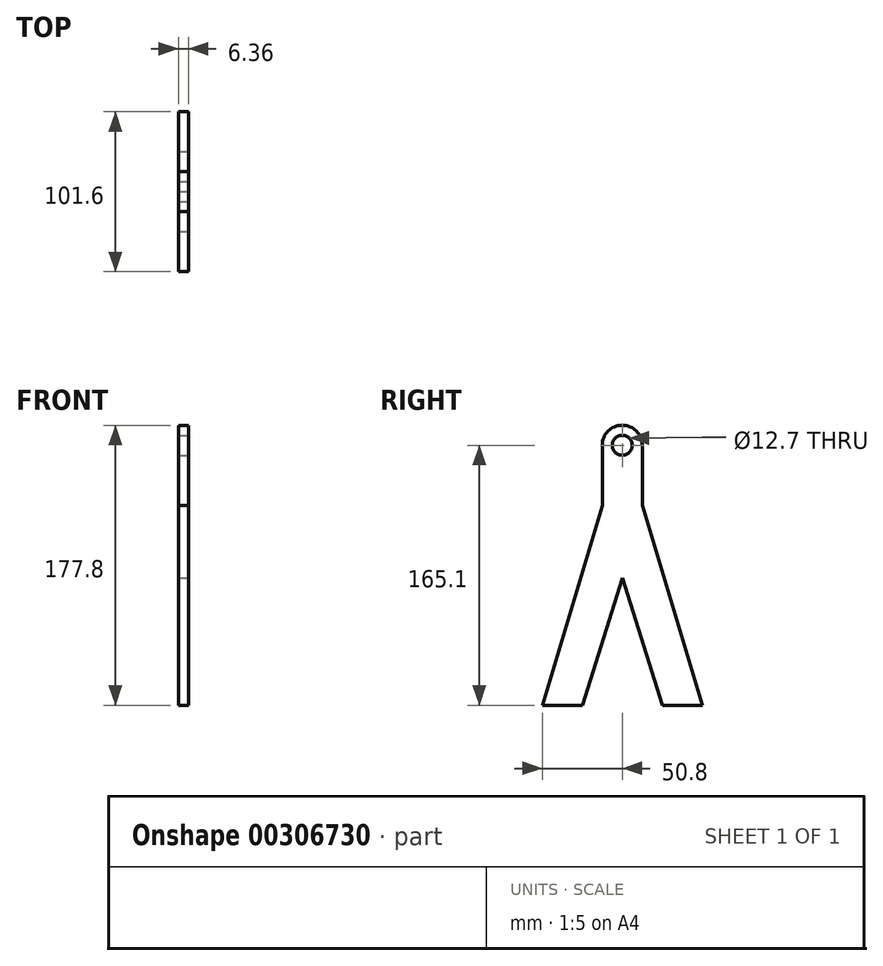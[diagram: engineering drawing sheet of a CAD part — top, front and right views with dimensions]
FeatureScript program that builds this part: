
annotation { "Feature Type Name" : "Feature", "Feature Type Description" : "" }
export const myFeature = defineFeature(function(context is Context, id is Id, definition is map)
    precondition{}
    {
        {
            var Q0;
            Q0=qCreatedBy(makeId("Top.planeOp"),FACE);
            var sketch = newSketch(context, id + "F0", { "sketchPlane" : qUnion([Q0])});
            skLineSegment(sketch, "E0.bottom", {"start": v(3.18, 50.8) * mm, "end": v(-3.17, 50.8) * mm});
            skLineSegment(sketch, "E0.top", {"start": v(3.18, -50.8) * mm, "end": v(-3.17, -50.8) * mm});
            skLineSegment(sketch, "E0.left", {"start": v(3.18, 50.8) * mm, "end": v(3.18, -50.8) * mm});
            skLineSegment(sketch, "E0.right", {"start": v(-3.17, 50.8) * mm, "end": v(-3.17, -50.8) * mm});
            skPoint(sketch, "E0.middle", {"position": v(0, 0) * mm});
            skLineSegment(sketch, "E1.bottom", {"start": v(-3.17, 12.7) * mm, "end": v(3.18, 12.7) * mm});
            skLineSegment(sketch, "E1.top", {"start": v(-3.18, -12.7) * mm, "end": v(3.17, -12.7) * mm});
            skLineSegment(sketch, "E1.left", {"start": v(-3.17, 12.7) * mm, "end": v(-3.18, -12.7) * mm});
            skLineSegment(sketch, "E1.right", {"start": v(3.18, 12.7) * mm, "end": v(3.17, -12.7) * mm});
            skSolve(sketch);
        }
        {
            var Q0;
            Q0=makeQuery(id+"F0.imprint","IMPRINT",FACE,{"disambiguationData":[TD([[makeQuery(id+"F0.imprint","IMPRINT",EDGE,{"derivedFrom":sQuery(id+"F0.wireOp",EDGE,"E1.bottom")}),-1.0]])]});
            extrude(context, id + "F1", {"entities" : qUnion([Q0]), "depth" : 177.8 * mm});
        }
        {
            var Q0;
            Q0=makeQuery(id+"F0.imprint","IMPRINT",FACE,{"disambiguationData":[TD([[makeQuery(id+"F0.imprint","IMPRINT",EDGE,{"derivedFrom":sQuery(id+"F0.wireOp",EDGE,"E0.bottom")}),1.0]])]});
            var Q1;
            {var subQ0=sQuery(id+"F0.wireOp",EDGE,"E0.top");Q1=makeQuery(id+"F0.imprint","IMPRINT",FACE,{"disambiguationData":[TD([[makeQuery(id+"F0.imprint","IMPRINT",EDGE,{"derivedFrom":subQ0}),-1.0]])]});}
            extrude(context, id + "F2", {"entities" : qUnion([Q0, Q1]), "operationType" : NewBodyOperationType.ADD, "depth" : 50.8 * mm});
        }
        {
            var Q0;
            Q0=qCreatedBy(makeId("Right.planeOp"),FACE);
            var sketch = newSketch(context, id + "F3", { "sketchPlane" : qUnion([Q0])});
            skCircle(sketch, "E2", {"center": v(0, 165.1) * mm, "radius": 6.35 * mm});
            skSolve(sketch);
        }
        {
            var Q0;
            Q0=sQuery(id+"F3.wireOp",VERTEX,"E2.center");
            var Q1;
            Q1=makeQuery(id+"F1.opExtrude","SWEPT_BODY",BODY,{"disambiguationData":[OSD([sQuery(id+"F0.wireOp",EDGE,"E1.bottom"),sQuery(id+"F0.wireOp",EDGE,"E1.top"),sQuery(id+"F0.wireOp",EDGE,"E1.left"),sQuery(id+"F0.wireOp",EDGE,"E1.right")])]});
            hole(context, id + "F4", {"style" : HoleStyle.SIMPLE, "endStyle" : HoleEndStyle.THROUGH, "holeDiameter" : 12.7 * mm, "tappedDepth" : 12.7 * mm, "tapClearance" : 3, "locations" : qUnion([Q0]), "scope" : qUnion([Q1])});
        }
        {
            var Q0;
            Q0=sQuery(id+"F3.wireOp",VERTEX,"E2.center");
            var Q1;
            Q1=makeQuery(id+"F1.opExtrude","SWEPT_BODY",BODY,{"disambiguationData":[OSD([sQuery(id+"F0.wireOp",EDGE,"E1.bottom"),sQuery(id+"F0.wireOp",EDGE,"E1.top"),sQuery(id+"F0.wireOp",EDGE,"E1.left"),sQuery(id+"F0.wireOp",EDGE,"E1.right")])]});
            hole(context, id + "F5", {"style" : HoleStyle.SIMPLE, "endStyle" : HoleEndStyle.THROUGH, "oppositeDirection" : true, "holeDiameter" : 12.7 * mm, "tappedDepth" : 12.7 * mm, "tapClearance" : 3, "locations" : qUnion([Q0]), "scope" : qUnion([Q1])});
        }
        {
            var Q0;
            Q0=makeQuery(id+"F1.opExtrude","CAP_EDGE",EDGE,{"disambiguationData":[OSD([sQuery(id+"F0.wireOp",EDGE,"E1.top")])],"isStart":false});
            var Q1;
            Q1=makeQuery(id+"F1.opExtrude","CAP_EDGE",EDGE,{"disambiguationData":[OSD([sQuery(id+"F0.wireOp",EDGE,"E1.bottom")])],"isStart":false});
            fillet(context, id + "F6", {"entities" : qUnion([Q0, Q1]), "radius" : 12.7 * mm, "tangentPropagation" : true, "allowEdgeOverflow" : false});
        }
        {
            var Q0;
            {var subQ0=sQuery(id+"F0.wireOp",EDGE,"E0.top");Q0=makeQuery(id+"F0.imprint","IMPRINT",FACE,{"disambiguationData":[TD([[makeQuery(id+"F0.imprint","IMPRINT",EDGE,{"derivedFrom":subQ0}),-1.0]])]});}
            var Q1;
            {var subQ0=sQuery(id+"F0.wireOp",EDGE,"E0.bottom");Q1=makeQuery(id+"F0.imprint","IMPRINT",FACE,{"disambiguationData":[TD([[makeQuery(id+"F0.imprint","IMPRINT",EDGE,{"derivedFrom":subQ0}),1.0]])]});}
            extrude(context, id + "F7", {"entities" : qUnion([Q0, Q1]), "operationType" : NewBodyOperationType.ADD, "oppositeDirection" : true, "depth" : -127 * mm});
        }
        {
            var Q0;
            Q0=makeQuery(id+"F7.opExtrude","CAP_EDGE",EDGE,{"disambiguationData":[OSD([sQuery(id+"F0.wireOp",EDGE,"E0.bottom")])],"isStart":false});
            chamfer(context, id + "F8", {"entities" : qUnion([Q0]), "chamferType" : ChamferType.TWO_OFFSETS, "width1" : 38.1 * mm, "oppositeDirection" : false, "width2" : 127 * mm, "tangentPropagation" : true});
        }
        {
            var Q0;
            Q0=makeQuery(id+"F7.opExtrude","CAP_EDGE",EDGE,{"disambiguationData":[OSD([sQuery(id+"F0.wireOp",EDGE,"E0.top")])],"isStart":false});
            chamfer(context, id + "F9", {"entities" : qUnion([Q0]), "chamferType" : ChamferType.TWO_OFFSETS, "width1" : 127 * mm, "oppositeDirection" : false, "width2" : 38.1 * mm, "tangentPropagation" : true});
        }
        {
            var Q0;
            {var subQ0=sQuery(id+"F0.wireOp",EDGE,"E0.left");var subQ1=sQuery(id+"F0.wireOp",EDGE,"E1.right");var subQ2=makeQuery(id+"F0.imprint","IMPRINT",EDGE,{"disambiguationData":[TD([[makeQuery(id+"F0.imprint","INTERSECT",VERTEX,{"derivedFrom":[sQuery(id+"F0.wireOp",EDGE,"E0.top"),subQ0]}),1.0]])],"derivedFrom":subQ0});var subQ3=makeQuery(id+"F0.imprint","IMPRINT",EDGE,{"disambiguationData":[TD([[makeQuery(id+"F0.imprint","INTERSECT",VERTEX,{"derivedFrom":[sQuery(id+"F0.wireOp",EDGE,"E0.bottom"),subQ0]}),-1.0]])],"derivedFrom":subQ0});Q0=makeQuery(id+"F7.boolean.opBoolean","MERGE",FACE,{"derivedFrom":[makeQuery(id+"F2.boolean.opBoolean","MERGE",FACE,{"derivedFrom":[makeQuery(id+"F1.opExtrude","SWEPT_FACE",FACE,{"disambiguationData":[OSD([subQ1])]}),makeQuery(id+"F2.opExtrude","SWEPT_FACE",FACE,{"disambiguationData":[OSD([subQ0]),TDD([subQ3])]}),makeQuery(id+"F2.opExtrude","SWEPT_FACE",FACE,{"disambiguationData":[OSD([subQ0]),TDD([subQ2])]})]}),makeQuery(id+"F7.opExtrude","SWEPT_FACE",FACE,{"disambiguationData":[OSD([subQ0]),TDD([subQ3])]}),makeQuery(id+"F7.opExtrude","SWEPT_FACE",FACE,{"disambiguationData":[OSD([subQ0]),TDD([subQ2])]})]});}
            var sketch = newSketch(context, id + "F10", { "sketchPlane" : qUnion([Q0])});
            skLineSegment(sketch, "E3", {"start": v(0, 80.95) * mm, "end": v(25.4, 0) * mm});
            skLineSegment(sketch, "E4", {"start": v(25.4, 0) * mm, "end": v(-25.4, 0) * mm});
            skLineSegment(sketch, "E5", {"start": v(-25.4, 0) * mm, "end": v(0, 80.95) * mm});
            skPoint(sketch, "E6", {"position": v(0, 80.95) * mm});
            skSolve(sketch);
        }
        {
            var Q0;
            Q0 = qSketchRegion(id + "F10", true);
            extrude(context, id + "F11", {"entities" : qUnion([Q0]), "operationType" : NewBodyOperationType.REMOVE, "oppositeDirection" : true, "depth" : 25.4 * mm});
        }
    });
